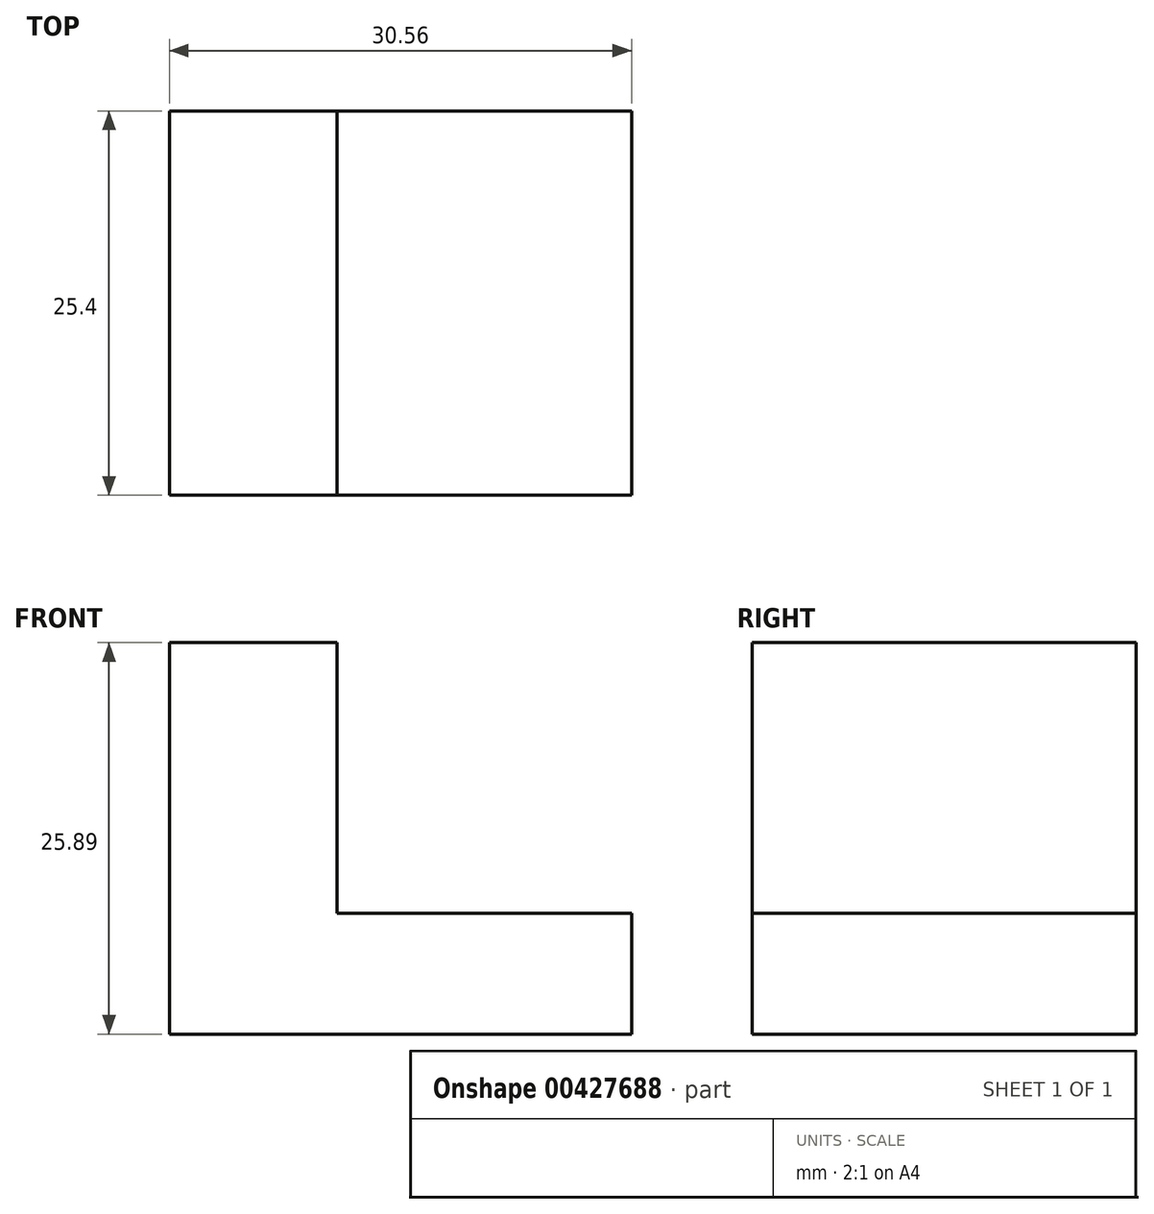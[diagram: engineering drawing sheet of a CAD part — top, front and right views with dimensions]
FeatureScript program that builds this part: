
annotation { "Feature Type Name" : "Feature", "Feature Type Description" : "" }
export const myFeature = defineFeature(function(context is Context, id is Id, definition is map)
    precondition{}
    {
        {
            var Q0;
            Q0=qCreatedBy(makeId("Front.planeOp"),FACE);
            var sketch = newSketch(context, id + "F0", { "sketchPlane" : qUnion([Q0])});
            skLineSegment(sketch, "E0", {"start": v(0, 0) * mm, "end": v(30.56, 0) * mm});
            skLineSegment(sketch, "E1", {"start": v(30.56, 0) * mm, "end": v(30.56, 5.84) * mm});
            skLineSegment(sketch, "E2", {"start": v(30.56, 5.84) * mm, "end": v(30.56, 7.98) * mm});
            skLineSegment(sketch, "E3", {"start": v(30.56, 7.98) * mm, "end": v(11.1, 7.98) * mm});
            skLineSegment(sketch, "E4", {"start": v(11.1, 7.98) * mm, "end": v(11.1, 25.9) * mm});
            skLineSegment(sketch, "E5", {"start": v(11.1, 25.9) * mm, "end": v(0, 25.9) * mm});
            skLineSegment(sketch, "E6", {"start": v(0, 25.9) * mm, "end": v(0, 0) * mm});
            skLineSegment(sketch, "E7", {"start": v(30.56, 0) * mm, "end": v(0, 0) * mm});
            skSolve(sketch);
        }
        {
            var Q0;
            Q0 = qSketchRegion(id + "F0", true);
            extrude(context, id + "F1", {"entities" : qUnion([Q0]), "depth" : 25.4 * mm});
        }
    });
